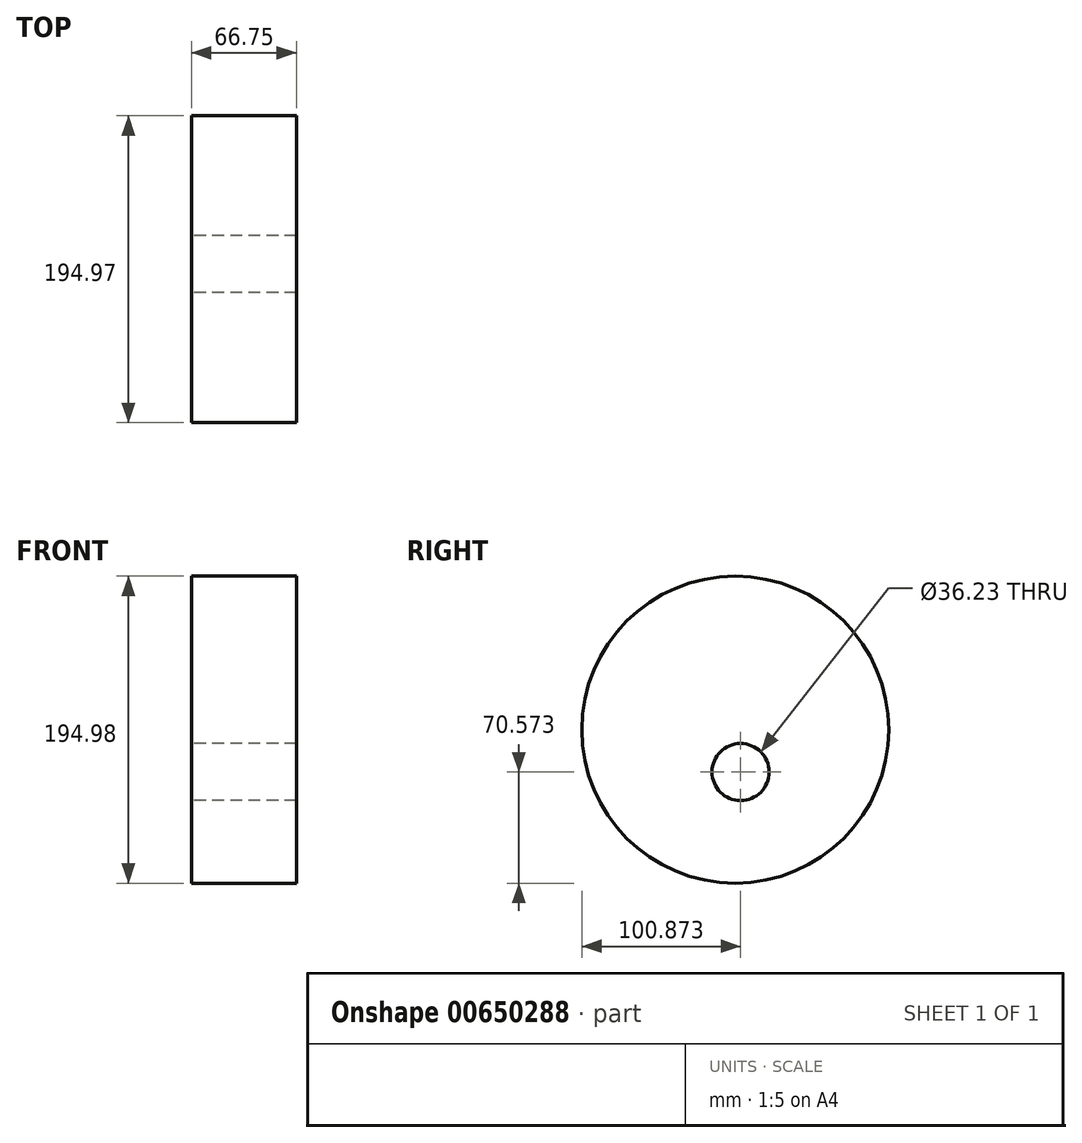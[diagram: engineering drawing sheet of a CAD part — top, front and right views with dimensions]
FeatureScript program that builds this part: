
annotation { "Feature Type Name" : "Feature", "Feature Type Description" : "" }
export const myFeature = defineFeature(function(context is Context, id is Id, definition is map)
    precondition{}
    {
        {
            var Q0;
            Q0=qCreatedBy(makeId("Right.planeOp"),FACE);
            var sketch = newSketch(context, id + "F0", { "sketchPlane" : qUnion([Q0])});
            skCircle(sketch, "E0", {"center": v(-49.87, 0) * mm, "radius": 97.49 * mm});
            skCircle(sketch, "E1", {"center": v(-46.49, -26.92) * mm, "radius": 18.12 * mm});
            skSolve(sketch);
        }
        {
            var Q0;
            Q0 = qSketchRegion(id + "F0", true);
            extrude(context, id + "F1", {"entities" : qUnion([Q0]), "depth" : 66.75 * mm, "offsetDistance" : 25.4 * mm});
        }
    });
